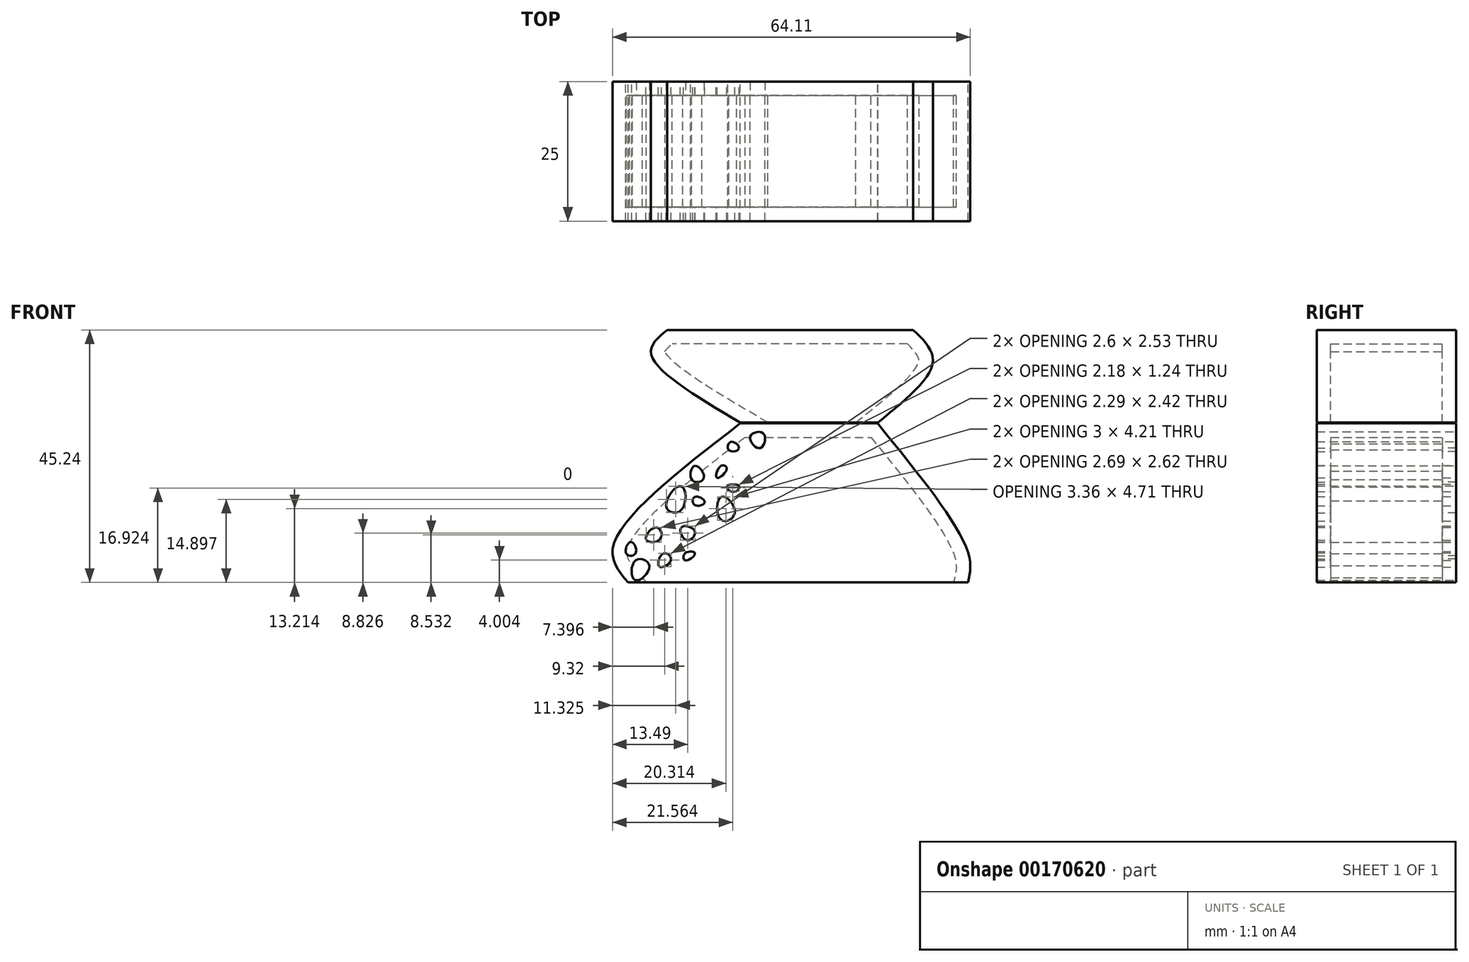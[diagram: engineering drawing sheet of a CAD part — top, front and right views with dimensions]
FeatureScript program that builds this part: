
annotation { "Feature Type Name" : "Feature", "Feature Type Description" : "" }
export const myFeature = defineFeature(function(context is Context, id is Id, definition is map)
    precondition{}
    {
        {
            var Q0;
            Q0=qCreatedBy(makeId("Front.planeOp"),FACE);
            var sketch = newSketch(context, id + "F0", { "sketchPlane" : qUnion([Q0])});
            skLineSegment(sketch, "E0", {"start": v(-34.5, 11.25) * mm, "end": v(-9.9, 11.25) * mm});
            skLineSegment(sketch, "E1", {"start": v(-54.6, -17.25) * mm, "end": v(6.3, -17.25) * mm});
            skFitSpline(sketch, "E2", {"points": [v(-9.9, 11.25) * mm, v(6.3, -11.85) * mm, v(6.3, -17.25) * mm], "startDerivative": vector(31.39, -38.58) * mm, "endDerivative": vector(-3.54, -15.4) * mm});
            skFitSpline(sketch, "E3", {"points": [v(-34.5, 11.25) * mm, v(-57.3, -10.95) * mm, v(-54.6, -17.25) * mm], "startDerivative": vector(-47.7, -36.82) * mm, "endDerivative": vector(15.16, -17.87) * mm});
            skSolve(sketch);
        }
        {
            var Q0;
            Q0 = qSketchRegion(id + "F0", true);
            extrude(context, id + "F1", {"entities" : qUnion([Q0]), "depth" : 25 * mm});
        }
        {
            var Q0;
            Q0=makeQuery(id+"F1.opExtrude","SWEPT_FACE",FACE,{"disambiguationData":[OSD([sQuery(id+"F0.wireOp",EDGE,"E1")])]});
            shell(context, id + "F2", {"entities" : qUnion([Q0]), "thickness" : 2.5 * mm});
        }
        {
            var Q0;
            Q0=qCreatedBy(makeId("Front.planeOp"),FACE);
            var sketch = newSketch(context, id + "F3", { "sketchPlane" : qUnion([Q0])});
            skFitSpline(sketch, "E4", {"points": [v(-34.73, 6.82) * mm, v(-36.5, 6.4) * mm, v(-36.24, 7.92) * mm, v(-34.73, 6.82) * mm]});
            skFitSpline(sketch, "E5", {"points": [v(-37.93, 3.62) * mm, v(-36.92, 3.12) * mm, v(-38.68, 1.52) * mm, v(-37.93, 3.62) * mm]});
            skFitSpline(sketch, "E6", {"points": [v(-42.64, 3.62) * mm, v(-41.04, 1.43) * mm, v(-43.15, 1.1) * mm, v(-42.64, 3.62) * mm]});
            skFitSpline(sketch, "E7", {"points": [v(-37.93, -1.93) * mm, v(-35.49, -4.71) * mm, v(-37.93, -6.06) * mm, v(-37.93, -1.93) * mm]});
            skFitSpline(sketch, "E8", {"points": [v(-42.64, -1.93) * mm, v(-42.64, -3.36) * mm, v(-40.87, -2.86) * mm, v(-42.64, -1.93) * mm]});
            skFitSpline(sketch, "E9", {"points": [v(-36.92, 0) * mm, v(-35.65, -1) * mm, v(-34.73, 0) * mm, v(-36.92, 0) * mm]});
            skFitSpline(sketch, "E10", {"points": [v(-45.08, 0) * mm, v(-45.08, -4.3) * mm, v(-47.78, -3.7) * mm, v(-45.08, 0) * mm]});
            skFitSpline(sketch, "E11", {"points": [v(-45.08, -7.4) * mm, v(-44.07, -9.68) * mm, v(-42.64, -8.08) * mm, v(-45.08, -7.4) * mm]});
            skFitSpline(sketch, "E12", {"points": [v(-49.46, -7.4) * mm, v(-48.87, -9.5) * mm, v(-51.4, -9.5) * mm, v(-49.46, -7.4) * mm]});
            skFitSpline(sketch, "E13", {"points": [v(-48.2, -12.04) * mm, v(-46.93, -13.3) * mm, v(-49.04, -14.4) * mm, v(-48.2, -12.04) * mm]});
            skFitSpline(sketch, "E14", {"points": [v(-53.25, -13.3) * mm, v(-50.8, -14.3) * mm, v(-53.33, -16.83) * mm, v(-53.25, -13.3) * mm]});
            skFitSpline(sketch, "E15", {"points": [v(-54.1, -10.01) * mm, v(-53.25, -12.04) * mm, v(-54.93, -12.04) * mm, v(-54.1, -10.01) * mm]});
            skFitSpline(sketch, "E16", {"points": [v(-44.33, -13.3) * mm, v(-42.64, -12.04) * mm, v(-44.4, -12.04) * mm, v(-44.33, -13.3) * mm]});
            skFitSpline(sketch, "E17", {"points": [v(-32.7, 8.84) * mm, v(-30.94, 6.82) * mm, v(-30.35, 9.43) * mm, v(-32.7, 8.84) * mm]});
            skSolve(sketch);
        }
        {
            var Q0;
            Q0 = qSketchRegion(id + "F3", true);
            extrude(context, id + "F4", {"entities" : qUnion([Q0]), "operationType" : NewBodyOperationType.REMOVE, "depth" : 87.7 * mm});
        }
        {
            var Q0;
            Q0=qCreatedBy(makeId("Front.planeOp"),FACE);
            var sketch = newSketch(context, id + "F5", { "sketchPlane" : qUnion([Q0])});
            skLineSegment(sketch, "E18", {"start": v(-9.83, 11.41) * mm, "end": v(-34.5, 11.41) * mm});
            skLineSegment(sketch, "E19", {"start": v(-3.5, 28) * mm, "end": v(-47.61, 28) * mm});
            skFitSpline(sketch, "E20", {"points": [v(-9.83, 11.41) * mm, v(0, 22.27) * mm, v(-3.5, 28) * mm], "startDerivative": vector(23.98, 19.4) * mm, "endDerivative": vector(-13.75, 13.37) * mm});
            skFitSpline(sketch, "E21", {"points": [v(-34.5, 11.41) * mm, v(-50.48, 23.78) * mm, v(-47.61, 28) * mm], "startDerivative": vector(-34.82, 20.57) * mm, "endDerivative": vector(14, 11.6) * mm});
            skSolve(sketch);
        }
        {
            var Q0;
            Q0 = qSketchRegion(id + "F5", true);
            extrude(context, id + "F6", {"entities" : qUnion([Q0]), "depth" : 25 * mm});
        }
        {
            var Q0;
            Q0=makeQuery(id+"F6.opExtrude","SWEPT_FACE",FACE,{"disambiguationData":[OSD([sQuery(id+"F5.wireOp",EDGE,"E18")])]});
            shell(context, id + "F7", {"entities" : qUnion([Q0]), "thickness" : 2.5 * mm});
        }
        {
            var Q0;
            Q0=qCreatedBy(makeId("Front.planeOp"),FACE);
            var sketch = newSketch(context, id + "F8", { "sketchPlane" : qUnion([Q0])});
            skLineSegment(sketch, "E22", {"start": v(-6.16, 24.36) * mm, "end": v(-6.16, 22.48) * mm});
            skLineSegment(sketch, "E23", {"start": v(-6.16, 22.48) * mm, "end": v(-8.12, 22.48) * mm});
            skLineSegment(sketch, "E24", {"start": v(-8.12, 22.48) * mm, "end": v(-6.16, 24.36) * mm});
            skLineSegment(sketch, "E25", {"start": v(-11.06, 21.6) * mm, "end": v(-8.12, 19.27) * mm});
            skLineSegment(sketch, "E26", {"start": v(-8.12, 19.27) * mm, "end": v(-11.42, 19.27) * mm});
            skLineSegment(sketch, "E27", {"start": v(-11.42, 19.27) * mm, "end": v(-11.06, 21.6) * mm});
            skLineSegment(sketch, "E28", {"start": v(-11.06, 23.64) * mm, "end": v(-13.38, 23.64) * mm});
            skLineSegment(sketch, "E29", {"start": v(-13.38, 23.64) * mm, "end": v(-13.38, 21.6) * mm});
            skLineSegment(sketch, "E30", {"start": v(-13.38, 21.6) * mm, "end": v(-11.06, 23.64) * mm});
            skLineSegment(sketch, "E31", {"start": v(-12.22, 18.47) * mm, "end": v(-13.74, 20.43) * mm});
            skLineSegment(sketch, "E32", {"start": v(-13.74, 20.43) * mm, "end": v(-15.1, 19.38) * mm});
            skLineSegment(sketch, "E33", {"start": v(-15.1, 19.38) * mm, "end": v(-12.22, 18.47) * mm});
            skLineSegment(sketch, "E34", {"start": v(-9.81, 17.76) * mm, "end": v(-11.33, 16.58) * mm});
            skLineSegment(sketch, "E35", {"start": v(-11.33, 16.58) * mm, "end": v(-11.33, 15.08) * mm});
            skLineSegment(sketch, "E36", {"start": v(-11.33, 15.08) * mm, "end": v(-9.81, 17.76) * mm});
            skLineSegment(sketch, "E37", {"start": v(-13.65, 15.08) * mm, "end": v(-16.41, 15.08) * mm});
            skLineSegment(sketch, "E38", {"start": v(-16.41, 15.08) * mm, "end": v(-15.1, 17.76) * mm});
            skLineSegment(sketch, "E39", {"start": v(-15.1, 17.76) * mm, "end": v(-13.65, 15.08) * mm});
            skLineSegment(sketch, "E40", {"start": v(-15.1, 12.05) * mm, "end": v(-15.1, 14.19) * mm});
            skLineSegment(sketch, "E41", {"start": v(-15.1, 14.19) * mm, "end": v(-17.8, 12.1) * mm});
            skLineSegment(sketch, "E42", {"start": v(-17.8, 12.1) * mm, "end": v(-15.1, 12.05) * mm});
            skLineSegment(sketch, "E43", {"start": v(-13.65, 14.53) * mm, "end": v(-14.53, 13.07) * mm});
            skLineSegment(sketch, "E44", {"start": v(-14.53, 13.07) * mm, "end": v(-13.07, 12.7) * mm});
            skLineSegment(sketch, "E45", {"start": v(-13.07, 12.7) * mm, "end": v(-13.65, 14.53) * mm});
            skLineSegment(sketch, "E46", {"start": v(-12.22, 17) * mm, "end": v(-13.1, 16.33) * mm});
            skLineSegment(sketch, "E47", {"start": v(-13.1, 16.33) * mm, "end": v(-13.6, 17.98) * mm});
            skLineSegment(sketch, "E48", {"start": v(-13.6, 17.98) * mm, "end": v(-12.22, 17) * mm});
            skLineSegment(sketch, "E49", {"start": v(-8.8, 23.36) * mm, "end": v(-9.17, 22.18) * mm});
            skLineSegment(sketch, "E50", {"start": v(-9.17, 22.18) * mm, "end": v(-10.51, 23.24) * mm});
            skLineSegment(sketch, "E51", {"start": v(-10.51, 23.24) * mm, "end": v(-8.8, 23.36) * mm});
            skLineSegment(sketch, "E52", {"start": v(-7.11, 22.18) * mm, "end": v(-9.17, 21.09) * mm});
            skLineSegment(sketch, "E53", {"start": v(-9.17, 21.09) * mm, "end": v(-7.4, 20.37) * mm});
            skLineSegment(sketch, "E54", {"start": v(-7.4, 20.37) * mm, "end": v(-7.11, 22.18) * mm});
            skLineSegment(sketch, "E55", {"start": v(-5.05, 21.09) * mm, "end": v(-6.48, 19.27) * mm});
            skLineSegment(sketch, "E56", {"start": v(-6.48, 19.27) * mm, "end": v(-6.48, 22.18) * mm});
            skLineSegment(sketch, "E57", {"start": v(-6.48, 22.18) * mm, "end": v(-5.05, 21.09) * mm});
            skSolve(sketch);
        }
        {
            var Q0;
            Q0=makeQuery(id+"F8.imprint","IMPRINT",FACE,{"disambiguationData":[TD([[makeQuery(id+"F8.imprint","IMPRINT",EDGE,{"derivedFrom":sQuery(id+"F8.wireOp",EDGE,"E28")}),1.0]])]});
            var Q1;
            Q1=makeQuery(id+"F8.imprint","IMPRINT",FACE,{"disambiguationData":[TD([[makeQuery(id+"F8.imprint","IMPRINT",EDGE,{"derivedFrom":sQuery(id+"F8.wireOp",EDGE,"E31")}),1.0]])]});
            var Q2;
            Q2=makeQuery(id+"F8.imprint","IMPRINT",FACE,{"disambiguationData":[TD([[makeQuery(id+"F8.imprint","IMPRINT",EDGE,{"derivedFrom":sQuery(id+"F8.wireOp",EDGE,"E37")}),-1.0]])]});
            var Q3;
            Q3=makeQuery(id+"F8.imprint","IMPRINT",FACE,{"disambiguationData":[TD([[makeQuery(id+"F8.imprint","IMPRINT",EDGE,{"derivedFrom":sQuery(id+"F8.wireOp",EDGE,"E43")}),1.0]])]});
            var Q4;
            Q4=makeQuery(id+"F8.imprint","IMPRINT",FACE,{"disambiguationData":[TD([[makeQuery(id+"F8.imprint","IMPRINT",EDGE,{"derivedFrom":sQuery(id+"F8.wireOp",EDGE,"E40")}),1.0]])]});
            var Q5;
            Q5=makeQuery(id+"F8.imprint","IMPRINT",FACE,{"disambiguationData":[TD([[makeQuery(id+"F8.imprint","IMPRINT",EDGE,{"derivedFrom":sQuery(id+"F8.wireOp",EDGE,"E46")}),-1.0]])]});
            var Q6;
            Q6=makeQuery(id+"F8.imprint","IMPRINT",FACE,{"disambiguationData":[TD([[makeQuery(id+"F8.imprint","IMPRINT",EDGE,{"derivedFrom":sQuery(id+"F8.wireOp",EDGE,"E34")}),1.0]])]});
            var Q7;
            Q7=makeQuery(id+"F8.imprint","IMPRINT",FACE,{"disambiguationData":[TD([[makeQuery(id+"F8.imprint","IMPRINT",EDGE,{"derivedFrom":sQuery(id+"F8.wireOp",EDGE,"E25")}),-1.0]])]});
            var Q8;
            Q8=makeQuery(id+"F8.imprint","IMPRINT",FACE,{"disambiguationData":[TD([[makeQuery(id+"F8.imprint","IMPRINT",EDGE,{"derivedFrom":sQuery(id+"F8.wireOp",EDGE,"E52")}),1.0]])]});
            var Q9;
            Q9=makeQuery(id+"F8.imprint","IMPRINT",FACE,{"disambiguationData":[TD([[makeQuery(id+"F8.imprint","IMPRINT",EDGE,{"derivedFrom":sQuery(id+"F8.wireOp",EDGE,"E22")}),-1.0]])]});
            var Q10;
            Q10=makeQuery(id+"F8.imprint","IMPRINT",FACE,{"disambiguationData":[TD([[makeQuery(id+"F8.imprint","IMPRINT",EDGE,{"derivedFrom":sQuery(id+"F8.wireOp",EDGE,"E55")}),-1.0]])]});
            var Q11;
            Q11=makeQuery(id+"F8.imprint","IMPRINT",FACE,{"disambiguationData":[TD([[makeQuery(id+"F8.imprint","IMPRINT",EDGE,{"derivedFrom":sQuery(id+"F8.wireOp",EDGE,"E49")}),-1.0]])]});
            extrude(context, id + "F9", {"entities" : qUnion([Q0, Q1, Q2, Q3, Q4, Q5, Q6, Q7, Q8, Q9, Q10, Q11]), "operationType" : NewBodyOperationType.REMOVE, "oppositeDirection" : true, "depth" : 25 * mm});
        }
    });
